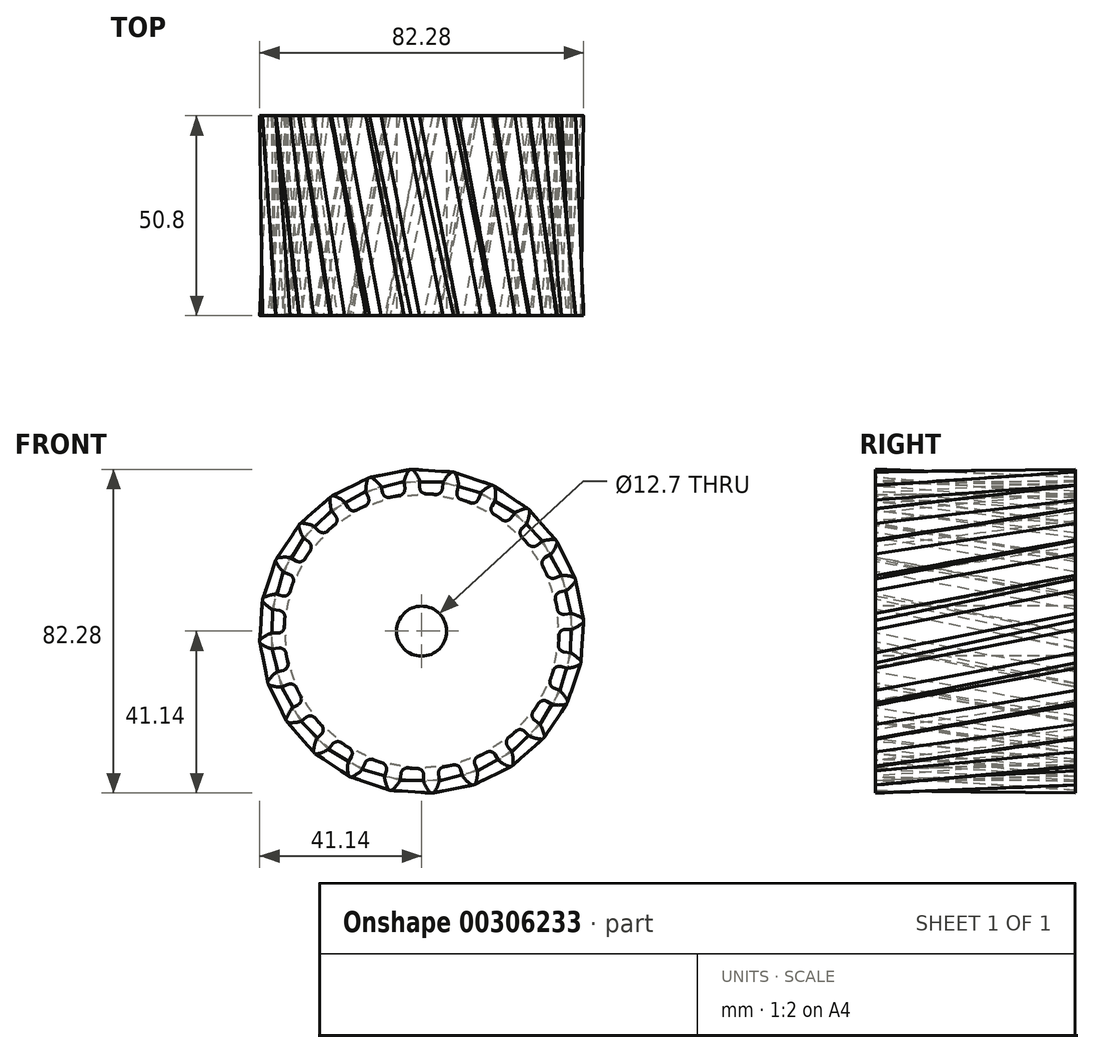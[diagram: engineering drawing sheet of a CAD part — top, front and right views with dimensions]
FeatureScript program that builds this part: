
annotation { "Feature Type Name" : "Feature", "Feature Type Description" : "" }
export const myFeature = defineFeature(function(context is Context, id is Id, definition is map)
    precondition{}
    {
        {
            var Q0;
            Q0=qCreatedBy(makeId("Front.planeOp"),FACE);
            var sketch = newSketch(context, id + "F0", { "sketchPlane" : qUnion([Q0])});
            skArc(sketch, "E0", {"start": v(-5.62, 34.47) * mm, "mid": v(-6.82, 34.25) * mm, "end": v(-8, 34) * mm});
            skLineSegment(sketch, "E1", {"start": v(0, 0) * mm, "end": v(-3.65, 55.58) * mm, "construction": true});
            skLineSegment(sketch, "E2", {"start": v(-2.53, 41.14) * mm, "end": v(-2.7, 41.14) * mm});
            skLineSegment(sketch, "E3", {"start": v(-0.5, 38.26) * mm, "end": v(-0.49, 36.5) * mm});
            skArc(sketch, "E4.trimOffspring", {"start": v(-0.5, 38.26) * mm, "mid": v(-1.2, 39.69) * mm, "end": v(-2.14, 40.97) * mm});
            skLineSegment(sketch, "E5.MirrorCS", {"start": v(-2.87, 41.12) * mm, "end": v(-2.7, 41.14) * mm});
            skArc(sketch, "E6.MirrorCS", {"start": v(-4.5, 38) * mm, "mid": v(-4, 39.5) * mm, "end": v(-3.23, 40.9) * mm});
            skLineSegment(sketch, "E7.MirrorCS", {"start": v(-4.5, 38) * mm, "end": v(-4.29, 36.25) * mm});
            skPoint(sketch, "E8.orphan", {"position": v(-3.92, 33.37) * mm});
            skPoint(sketch, "E9.orphan", {"position": v(-0.48, 33.6) * mm});
            skPoint(sketch, "E10.visualSharp", {"position": v(-4.08, 34.69) * mm});
            skArc(sketch, "E10.filletArc", {"start": v(-5.62, 34.47) * mm, "mid": v(-4.59, 35.1) * mm, "end": v(-4.29, 36.25) * mm});
            skPoint(sketch, "E11.visualSharp", {"position": v(-0.48, 34.92) * mm});
            skArc(sketch, "E11.filletArc", {"start": v(-0.49, 36.5) * mm, "mid": v(-0.03, 35.4) * mm, "end": v(1.06, 34.9) * mm});
            skPoint(sketch, "E12.visualSharp", {"position": v(-2.3, 41.14) * mm});
            skArc(sketch, "E12.filletArc", {"start": v(-2.14, 40.97) * mm, "mid": v(-2.32, 41.1) * mm, "end": v(-2.53, 41.14) * mm});
            skPoint(sketch, "E13.visualSharp", {"position": v(-3.1, 41.1) * mm});
            skArc(sketch, "E13.filletArc", {"start": v(-2.87, 41.12) * mm, "mid": v(-3.07, 41.05) * mm, "end": v(-3.23, 40.9) * mm});
            skLineSegment(sketch, "E14.1.0", {"start": v(-13.42, 38.98) * mm, "end": v(-13.26, 39.04) * mm});
            skArc(sketch, "E14.1.1", {"start": v(-14.19, 35.54) * mm, "mid": v(-14.08, 37.12) * mm, "end": v(-13.7, 38.67) * mm});
            skLineSegment(sketch, "E14.1.2", {"start": v(-13.09, 39.09) * mm, "end": v(-13.26, 39.04) * mm});
            skArc(sketch, "E14.1.3", {"start": v(-14.35, 31.84) * mm, "mid": v(-13.52, 32.7) * mm, "end": v(-13.52, 33.9) * mm});
            skLineSegment(sketch, "E14.1.4", {"start": v(-14.19, 35.54) * mm, "end": v(-13.52, 33.9) * mm});
            skArc(sketch, "E14.1.5", {"start": v(-10.38, 36.83) * mm, "mid": v(-11.43, 38.02) * mm, "end": v(-12.67, 39.02) * mm});
            skLineSegment(sketch, "E14.1.6", {"start": v(-10.38, 36.83) * mm, "end": v(-9.92, 35.13) * mm});
            skArc(sketch, "E14.1.7", {"start": v(-9.92, 35.13) * mm, "mid": v(-9.2, 34.18) * mm, "end": v(-8, 34) * mm});
            skArc(sketch, "E14.1.8", {"start": v(-12.67, 39.02) * mm, "mid": v(-12.87, 39.1) * mm, "end": v(-13.09, 39.09) * mm});
            skArc(sketch, "E14.1.9", {"start": v(-13.42, 38.98) * mm, "mid": v(-13.6, 38.85) * mm, "end": v(-13.7, 38.67) * mm});
            skLineSegment(sketch, "E14.2.0", {"start": v(-23.05, 34.18) * mm, "end": v(-22.9, 34.28) * mm});
            skArc(sketch, "E14.2.1", {"start": v(-22.9, 30.65) * mm, "mid": v(-23.2, 32.21) * mm, "end": v(-23.24, 33.8) * mm});
            skLineSegment(sketch, "E14.2.2", {"start": v(-22.76, 34.37) * mm, "end": v(-22.9, 34.28) * mm});
            skArc(sketch, "E14.2.3", {"start": v(-22.1, 27.04) * mm, "mid": v(-21.52, 28.1) * mm, "end": v(-21.84, 29.25) * mm});
            skLineSegment(sketch, "E14.2.4", {"start": v(-22.9, 30.65) * mm, "end": v(-21.84, 29.25) * mm});
            skArc(sketch, "E14.2.5", {"start": v(-19.56, 32.89) * mm, "mid": v(-20.88, 33.77) * mm, "end": v(-22.34, 34.4) * mm});
            skLineSegment(sketch, "E14.2.6", {"start": v(-19.56, 32.89) * mm, "end": v(-18.67, 31.37) * mm});
            skArc(sketch, "E14.2.7", {"start": v(-18.67, 31.37) * mm, "mid": v(-17.73, 30.63) * mm, "end": v(-16.53, 30.76) * mm});
            skArc(sketch, "E14.2.8", {"start": v(-22.34, 34.4) * mm, "mid": v(-22.55, 34.43) * mm, "end": v(-22.76, 34.37) * mm});
            skArc(sketch, "E14.2.9", {"start": v(-23.05, 34.18) * mm, "mid": v(-23.19, 34.01) * mm, "end": v(-23.24, 33.8) * mm});
            skLineSegment(sketch, "E14.3.0", {"start": v(-31.1, 27.05) * mm, "end": v(-31, 27.18) * mm});
            skArc(sketch, "E14.3.1", {"start": v(-30.06, 23.68) * mm, "mid": v(-30.75, 25.1) * mm, "end": v(-31.2, 26.64) * mm});
            skLineSegment(sketch, "E14.3.2", {"start": v(-30.88, 27.3) * mm, "end": v(-31, 27.18) * mm});
            skArc(sketch, "E14.3.3", {"start": v(-28.34, 20.4) * mm, "mid": v(-28.06, 21.57) * mm, "end": v(-28.66, 22.6) * mm});
            skLineSegment(sketch, "E14.3.4", {"start": v(-30.06, 23.68) * mm, "end": v(-28.66, 22.6) * mm});
            skArc(sketch, "E14.3.5", {"start": v(-27.4, 26.7) * mm, "mid": v(-28.91, 27.21) * mm, "end": v(-30.48, 27.45) * mm});
            skLineSegment(sketch, "E14.3.6", {"start": v(-27.4, 26.7) * mm, "end": v(-26.16, 25.47) * mm});
            skArc(sketch, "E14.3.7", {"start": v(-26.16, 25.47) * mm, "mid": v(-25.05, 25) * mm, "end": v(-23.93, 25.44) * mm});
            skArc(sketch, "E14.3.8", {"start": v(-30.48, 27.45) * mm, "mid": v(-30.7, 27.42) * mm, "end": v(-30.88, 27.3) * mm});
            skArc(sketch, "E14.3.9", {"start": v(-31.1, 27.05) * mm, "mid": v(-31.2, 26.85) * mm, "end": v(-31.2, 26.64) * mm});
            skLineSegment(sketch, "E14.4.0", {"start": v(-37.05, 18.07) * mm, "end": v(-36.98, 18.23) * mm});
            skArc(sketch, "E14.4.1", {"start": v(-35.16, 15.1) * mm, "mid": v(-36.2, 16.3) * mm, "end": v(-37.03, 17.65) * mm});
            skLineSegment(sketch, "E14.4.2", {"start": v(-36.9, 18.38) * mm, "end": v(-36.98, 18.23) * mm});
            skArc(sketch, "E14.4.3", {"start": v(-32.66, 12.37) * mm, "mid": v(-32.69, 13.57) * mm, "end": v(-33.54, 14.42) * mm});
            skLineSegment(sketch, "E14.4.4", {"start": v(-35.16, 15.1) * mm, "end": v(-33.54, 14.42) * mm});
            skArc(sketch, "E14.4.5", {"start": v(-33.38, 18.7) * mm, "mid": v(-34.97, 18.8) * mm, "end": v(-36.55, 18.63) * mm});
            skLineSegment(sketch, "E14.4.6", {"start": v(-33.38, 18.7) * mm, "end": v(-31.86, 17.83) * mm});
            skArc(sketch, "E14.4.7", {"start": v(-31.86, 17.83) * mm, "mid": v(-30.67, 17.67) * mm, "end": v(-29.7, 18.38) * mm});
            skArc(sketch, "E14.4.8", {"start": v(-36.55, 18.63) * mm, "mid": v(-36.75, 18.54) * mm, "end": v(-36.9, 18.38) * mm});
            skArc(sketch, "E14.4.9", {"start": v(-37.05, 18.07) * mm, "mid": v(-37.08, 17.86) * mm, "end": v(-37.03, 17.65) * mm});
            skLineSegment(sketch, "E14.5.0", {"start": v(-40.46, 7.87) * mm, "end": v(-40.44, 8.04) * mm});
            skArc(sketch, "E14.5.1", {"start": v(-37.87, 5.48) * mm, "mid": v(-39.19, 6.37) * mm, "end": v(-40.34, 7.47) * mm});
            skLineSegment(sketch, "E14.5.2", {"start": v(-40.4, 8.2) * mm, "end": v(-40.44, 8.04) * mm});
            skArc(sketch, "E14.5.3", {"start": v(-34.75, 3.5) * mm, "mid": v(-35.09, 4.65) * mm, "end": v(-36.13, 5.24) * mm});
            skLineSegment(sketch, "E14.5.4", {"start": v(-37.87, 5.48) * mm, "end": v(-36.13, 5.24) * mm});
            skArc(sketch, "E14.5.5", {"start": v(-37.09, 9.43) * mm, "mid": v(-38.64, 9.1) * mm, "end": v(-40.13, 8.53) * mm});
            skLineSegment(sketch, "E14.5.6", {"start": v(-37.09, 9.43) * mm, "end": v(-35.38, 8.98) * mm});
            skArc(sketch, "E14.5.7", {"start": v(-35.38, 8.98) * mm, "mid": v(-34.2, 9.13) * mm, "end": v(-33.44, 10.06) * mm});
            skArc(sketch, "E14.5.8", {"start": v(-40.13, 8.53) * mm, "mid": v(-40.3, 8.4) * mm, "end": v(-40.4, 8.2) * mm});
            skArc(sketch, "E14.5.9", {"start": v(-40.46, 7.87) * mm, "mid": v(-40.44, 7.66) * mm, "end": v(-40.34, 7.47) * mm});
            skLineSegment(sketch, "E14.6.0", {"start": v(-41.12, -2.87) * mm, "end": v(-41.14, -2.7) * mm});
            skArc(sketch, "E14.6.1", {"start": v(-38, -4.5) * mm, "mid": v(-39.5, -4) * mm, "end": v(-40.9, -3.23) * mm});
            skLineSegment(sketch, "E14.6.2", {"start": v(-41.14, -2.53) * mm, "end": v(-41.14, -2.7) * mm});
            skArc(sketch, "E14.6.3", {"start": v(-34.47, -5.62) * mm, "mid": v(-35.1, -4.59) * mm, "end": v(-36.25, -4.29) * mm});
            skLineSegment(sketch, "E14.6.4", {"start": v(-38, -4.5) * mm, "end": v(-36.25, -4.29) * mm});
            skArc(sketch, "E14.6.5", {"start": v(-38.26, -0.5) * mm, "mid": v(-39.69, -1.2) * mm, "end": v(-40.97, -2.14) * mm});
            skLineSegment(sketch, "E14.6.6", {"start": v(-38.26, -0.5) * mm, "end": v(-36.5, -0.49) * mm});
            skArc(sketch, "E14.6.7", {"start": v(-36.5, -0.49) * mm, "mid": v(-35.4, -0.03) * mm, "end": v(-34.9, 1.06) * mm});
            skArc(sketch, "E14.6.8", {"start": v(-40.97, -2.14) * mm, "mid": v(-41.1, -2.32) * mm, "end": v(-41.14, -2.53) * mm});
            skArc(sketch, "E14.6.9", {"start": v(-41.12, -2.87) * mm, "mid": v(-41.05, -3.07) * mm, "end": v(-40.9, -3.23) * mm});
            skLineSegment(sketch, "E14.7.0", {"start": v(-38.98, -13.42) * mm, "end": v(-39.04, -13.26) * mm});
            skArc(sketch, "E14.7.1", {"start": v(-35.54, -14.19) * mm, "mid": v(-37.12, -14.08) * mm, "end": v(-38.67, -13.7) * mm});
            skLineSegment(sketch, "E14.7.2", {"start": v(-39.09, -13.09) * mm, "end": v(-39.04, -13.26) * mm});
            skArc(sketch, "E14.7.3", {"start": v(-31.84, -14.35) * mm, "mid": v(-32.7, -13.52) * mm, "end": v(-33.9, -13.52) * mm});
            skLineSegment(sketch, "E14.7.4", {"start": v(-35.54, -14.19) * mm, "end": v(-33.9, -13.52) * mm});
            skArc(sketch, "E14.7.5", {"start": v(-36.83, -10.38) * mm, "mid": v(-38.02, -11.43) * mm, "end": v(-39.02, -12.67) * mm});
            skLineSegment(sketch, "E14.7.6", {"start": v(-36.83, -10.38) * mm, "end": v(-35.13, -9.92) * mm});
            skArc(sketch, "E14.7.7", {"start": v(-35.13, -9.92) * mm, "mid": v(-34.18, -9.2) * mm, "end": v(-34, -8) * mm});
            skArc(sketch, "E14.7.8", {"start": v(-39.02, -12.67) * mm, "mid": v(-39.1, -12.87) * mm, "end": v(-39.09, -13.09) * mm});
            skArc(sketch, "E14.7.9", {"start": v(-38.98, -13.42) * mm, "mid": v(-38.85, -13.6) * mm, "end": v(-38.67, -13.7) * mm});
            skLineSegment(sketch, "E14.8.0", {"start": v(-34.18, -23.05) * mm, "end": v(-34.28, -22.9) * mm});
            skArc(sketch, "E14.8.1", {"start": v(-30.65, -22.9) * mm, "mid": v(-32.21, -23.2) * mm, "end": v(-33.8, -23.24) * mm});
            skLineSegment(sketch, "E14.8.2", {"start": v(-34.37, -22.76) * mm, "end": v(-34.28, -22.9) * mm});
            skArc(sketch, "E14.8.3", {"start": v(-27.04, -22.1) * mm, "mid": v(-28.1, -21.52) * mm, "end": v(-29.25, -21.84) * mm});
            skLineSegment(sketch, "E14.8.4", {"start": v(-30.65, -22.9) * mm, "end": v(-29.25, -21.84) * mm});
            skArc(sketch, "E14.8.5", {"start": v(-32.89, -19.56) * mm, "mid": v(-33.77, -20.88) * mm, "end": v(-34.4, -22.34) * mm});
            skLineSegment(sketch, "E14.8.6", {"start": v(-32.89, -19.56) * mm, "end": v(-31.37, -18.67) * mm});
            skArc(sketch, "E14.8.7", {"start": v(-31.37, -18.67) * mm, "mid": v(-30.63, -17.73) * mm, "end": v(-30.76, -16.53) * mm});
            skArc(sketch, "E14.8.8", {"start": v(-34.4, -22.34) * mm, "mid": v(-34.43, -22.55) * mm, "end": v(-34.37, -22.76) * mm});
            skArc(sketch, "E14.8.9", {"start": v(-34.18, -23.05) * mm, "mid": v(-34.01, -23.19) * mm, "end": v(-33.8, -23.24) * mm});
            skLineSegment(sketch, "E14.9.0", {"start": v(-27.05, -31.1) * mm, "end": v(-27.18, -31) * mm});
            skArc(sketch, "E14.9.1", {"start": v(-23.68, -30.06) * mm, "mid": v(-25.1, -30.75) * mm, "end": v(-26.64, -31.2) * mm});
            skLineSegment(sketch, "E14.9.2", {"start": v(-27.3, -30.88) * mm, "end": v(-27.18, -31) * mm});
            skArc(sketch, "E14.9.3", {"start": v(-20.4, -28.34) * mm, "mid": v(-21.57, -28.06) * mm, "end": v(-22.6, -28.66) * mm});
            skLineSegment(sketch, "E14.9.4", {"start": v(-23.68, -30.06) * mm, "end": v(-22.6, -28.66) * mm});
            skArc(sketch, "E14.9.5", {"start": v(-26.7, -27.4) * mm, "mid": v(-27.21, -28.91) * mm, "end": v(-27.45, -30.48) * mm});
            skLineSegment(sketch, "E14.9.6", {"start": v(-26.7, -27.4) * mm, "end": v(-25.47, -26.16) * mm});
            skArc(sketch, "E14.9.7", {"start": v(-25.47, -26.16) * mm, "mid": v(-25, -25.05) * mm, "end": v(-25.44, -23.93) * mm});
            skArc(sketch, "E14.9.8", {"start": v(-27.45, -30.48) * mm, "mid": v(-27.42, -30.7) * mm, "end": v(-27.3, -30.88) * mm});
            skArc(sketch, "E14.9.9", {"start": v(-27.05, -31.1) * mm, "mid": v(-26.85, -31.2) * mm, "end": v(-26.64, -31.2) * mm});
            skLineSegment(sketch, "E14.10.0", {"start": v(-18.07, -37.05) * mm, "end": v(-18.23, -36.98) * mm});
            skArc(sketch, "E14.10.1", {"start": v(-15.1, -35.16) * mm, "mid": v(-16.3, -36.2) * mm, "end": v(-17.65, -37.03) * mm});
            skLineSegment(sketch, "E14.10.2", {"start": v(-18.38, -36.9) * mm, "end": v(-18.23, -36.98) * mm});
            skArc(sketch, "E14.10.3", {"start": v(-12.37, -32.66) * mm, "mid": v(-13.57, -32.69) * mm, "end": v(-14.42, -33.54) * mm});
            skLineSegment(sketch, "E14.10.4", {"start": v(-15.1, -35.16) * mm, "end": v(-14.42, -33.54) * mm});
            skArc(sketch, "E14.10.5", {"start": v(-18.7, -33.38) * mm, "mid": v(-18.8, -34.97) * mm, "end": v(-18.63, -36.55) * mm});
            skLineSegment(sketch, "E14.10.6", {"start": v(-18.7, -33.38) * mm, "end": v(-17.83, -31.86) * mm});
            skArc(sketch, "E14.10.7", {"start": v(-17.83, -31.86) * mm, "mid": v(-17.67, -30.67) * mm, "end": v(-18.38, -29.7) * mm});
            skArc(sketch, "E14.10.8", {"start": v(-18.63, -36.55) * mm, "mid": v(-18.54, -36.75) * mm, "end": v(-18.38, -36.9) * mm});
            skArc(sketch, "E14.10.9", {"start": v(-18.07, -37.05) * mm, "mid": v(-17.86, -37.08) * mm, "end": v(-17.65, -37.03) * mm});
            skLineSegment(sketch, "E14.11.0", {"start": v(-7.87, -40.46) * mm, "end": v(-8.04, -40.44) * mm});
            skArc(sketch, "E14.11.1", {"start": v(-5.48, -37.87) * mm, "mid": v(-6.37, -39.19) * mm, "end": v(-7.47, -40.34) * mm});
            skLineSegment(sketch, "E14.11.2", {"start": v(-8.2, -40.4) * mm, "end": v(-8.04, -40.44) * mm});
            skArc(sketch, "E14.11.3", {"start": v(-3.5, -34.75) * mm, "mid": v(-4.65, -35.09) * mm, "end": v(-5.24, -36.13) * mm});
            skLineSegment(sketch, "E14.11.4", {"start": v(-5.48, -37.87) * mm, "end": v(-5.24, -36.13) * mm});
            skArc(sketch, "E14.11.5", {"start": v(-9.43, -37.09) * mm, "mid": v(-9.1, -38.64) * mm, "end": v(-8.53, -40.13) * mm});
            skLineSegment(sketch, "E14.11.6", {"start": v(-9.43, -37.09) * mm, "end": v(-8.98, -35.38) * mm});
            skArc(sketch, "E14.11.7", {"start": v(-8.98, -35.38) * mm, "mid": v(-9.13, -34.2) * mm, "end": v(-10.06, -33.44) * mm});
            skArc(sketch, "E14.11.8", {"start": v(-8.53, -40.13) * mm, "mid": v(-8.4, -40.3) * mm, "end": v(-8.2, -40.4) * mm});
            skArc(sketch, "E14.11.9", {"start": v(-7.87, -40.46) * mm, "mid": v(-7.66, -40.44) * mm, "end": v(-7.47, -40.34) * mm});
            skLineSegment(sketch, "E14.12.0", {"start": v(2.87, -41.12) * mm, "end": v(2.7, -41.14) * mm});
            skArc(sketch, "E14.12.1", {"start": v(4.5, -38) * mm, "mid": v(4, -39.5) * mm, "end": v(3.23, -40.9) * mm});
            skLineSegment(sketch, "E14.12.2", {"start": v(2.53, -41.14) * mm, "end": v(2.7, -41.14) * mm});
            skArc(sketch, "E14.12.3", {"start": v(5.62, -34.47) * mm, "mid": v(4.59, -35.1) * mm, "end": v(4.29, -36.25) * mm});
            skLineSegment(sketch, "E14.12.4", {"start": v(4.5, -38) * mm, "end": v(4.29, -36.25) * mm});
            skArc(sketch, "E14.12.5", {"start": v(0.5, -38.26) * mm, "mid": v(1.2, -39.69) * mm, "end": v(2.14, -40.97) * mm});
            skLineSegment(sketch, "E14.12.6", {"start": v(0.5, -38.26) * mm, "end": v(0.49, -36.5) * mm});
            skArc(sketch, "E14.12.7", {"start": v(0.49, -36.5) * mm, "mid": v(0.03, -35.4) * mm, "end": v(-1.06, -34.9) * mm});
            skArc(sketch, "E14.12.8", {"start": v(2.14, -40.97) * mm, "mid": v(2.32, -41.1) * mm, "end": v(2.53, -41.14) * mm});
            skArc(sketch, "E14.12.9", {"start": v(2.87, -41.12) * mm, "mid": v(3.07, -41.05) * mm, "end": v(3.23, -40.9) * mm});
            skLineSegment(sketch, "E14.13.0", {"start": v(13.42, -38.98) * mm, "end": v(13.26, -39.04) * mm});
            skArc(sketch, "E14.13.1", {"start": v(14.19, -35.54) * mm, "mid": v(14.08, -37.12) * mm, "end": v(13.7, -38.67) * mm});
            skLineSegment(sketch, "E14.13.2", {"start": v(13.09, -39.09) * mm, "end": v(13.26, -39.04) * mm});
            skArc(sketch, "E14.13.3", {"start": v(14.35, -31.84) * mm, "mid": v(13.52, -32.7) * mm, "end": v(13.52, -33.9) * mm});
            skLineSegment(sketch, "E14.13.4", {"start": v(14.19, -35.54) * mm, "end": v(13.52, -33.9) * mm});
            skArc(sketch, "E14.13.5", {"start": v(10.38, -36.83) * mm, "mid": v(11.43, -38.02) * mm, "end": v(12.67, -39.02) * mm});
            skLineSegment(sketch, "E14.13.6", {"start": v(10.38, -36.83) * mm, "end": v(9.92, -35.13) * mm});
            skArc(sketch, "E14.13.7", {"start": v(9.92, -35.13) * mm, "mid": v(9.2, -34.18) * mm, "end": v(8, -34) * mm});
            skArc(sketch, "E14.13.8", {"start": v(12.67, -39.02) * mm, "mid": v(12.87, -39.1) * mm, "end": v(13.09, -39.09) * mm});
            skArc(sketch, "E14.13.9", {"start": v(13.42, -38.98) * mm, "mid": v(13.6, -38.85) * mm, "end": v(13.7, -38.67) * mm});
            skLineSegment(sketch, "E14.14.0", {"start": v(23.05, -34.18) * mm, "end": v(22.9, -34.28) * mm});
            skArc(sketch, "E14.14.1", {"start": v(22.9, -30.65) * mm, "mid": v(23.2, -32.21) * mm, "end": v(23.24, -33.8) * mm});
            skLineSegment(sketch, "E14.14.2", {"start": v(22.76, -34.37) * mm, "end": v(22.9, -34.28) * mm});
            skArc(sketch, "E14.14.3", {"start": v(22.1, -27.04) * mm, "mid": v(21.52, -28.1) * mm, "end": v(21.84, -29.25) * mm});
            skLineSegment(sketch, "E14.14.4", {"start": v(22.9, -30.65) * mm, "end": v(21.84, -29.25) * mm});
            skArc(sketch, "E14.14.5", {"start": v(19.56, -32.89) * mm, "mid": v(20.88, -33.77) * mm, "end": v(22.34, -34.4) * mm});
            skLineSegment(sketch, "E14.14.6", {"start": v(19.56, -32.89) * mm, "end": v(18.67, -31.37) * mm});
            skArc(sketch, "E14.14.7", {"start": v(18.67, -31.37) * mm, "mid": v(17.73, -30.63) * mm, "end": v(16.53, -30.76) * mm});
            skArc(sketch, "E14.14.8", {"start": v(22.34, -34.4) * mm, "mid": v(22.55, -34.43) * mm, "end": v(22.76, -34.37) * mm});
            skArc(sketch, "E14.14.9", {"start": v(23.05, -34.18) * mm, "mid": v(23.19, -34.01) * mm, "end": v(23.24, -33.8) * mm});
            skLineSegment(sketch, "E14.15.0", {"start": v(31.1, -27.05) * mm, "end": v(31, -27.18) * mm});
            skArc(sketch, "E14.15.1", {"start": v(30.06, -23.68) * mm, "mid": v(30.75, -25.1) * mm, "end": v(31.2, -26.64) * mm});
            skLineSegment(sketch, "E14.15.2", {"start": v(30.88, -27.3) * mm, "end": v(31, -27.18) * mm});
            skArc(sketch, "E14.15.3", {"start": v(28.34, -20.4) * mm, "mid": v(28.06, -21.57) * mm, "end": v(28.66, -22.6) * mm});
            skLineSegment(sketch, "E14.15.4", {"start": v(30.06, -23.68) * mm, "end": v(28.66, -22.6) * mm});
            skArc(sketch, "E14.15.5", {"start": v(27.4, -26.7) * mm, "mid": v(28.91, -27.21) * mm, "end": v(30.48, -27.45) * mm});
            skLineSegment(sketch, "E14.15.6", {"start": v(27.4, -26.7) * mm, "end": v(26.16, -25.47) * mm});
            skArc(sketch, "E14.15.7", {"start": v(26.16, -25.47) * mm, "mid": v(25.05, -25) * mm, "end": v(23.93, -25.44) * mm});
            skArc(sketch, "E14.15.8", {"start": v(30.48, -27.45) * mm, "mid": v(30.7, -27.42) * mm, "end": v(30.88, -27.3) * mm});
            skArc(sketch, "E14.15.9", {"start": v(31.1, -27.05) * mm, "mid": v(31.2, -26.85) * mm, "end": v(31.2, -26.64) * mm});
            skLineSegment(sketch, "E14.16.0", {"start": v(37.05, -18.07) * mm, "end": v(36.98, -18.23) * mm});
            skArc(sketch, "E14.16.1", {"start": v(35.16, -15.1) * mm, "mid": v(36.2, -16.3) * mm, "end": v(37.03, -17.65) * mm});
            skLineSegment(sketch, "E14.16.2", {"start": v(36.9, -18.38) * mm, "end": v(36.98, -18.23) * mm});
            skArc(sketch, "E14.16.3", {"start": v(32.66, -12.37) * mm, "mid": v(32.69, -13.57) * mm, "end": v(33.54, -14.42) * mm});
            skLineSegment(sketch, "E14.16.4", {"start": v(35.16, -15.1) * mm, "end": v(33.54, -14.42) * mm});
            skArc(sketch, "E14.16.5", {"start": v(33.38, -18.7) * mm, "mid": v(34.97, -18.8) * mm, "end": v(36.55, -18.63) * mm});
            skLineSegment(sketch, "E14.16.6", {"start": v(33.38, -18.7) * mm, "end": v(31.86, -17.83) * mm});
            skArc(sketch, "E14.16.7", {"start": v(31.86, -17.83) * mm, "mid": v(30.67, -17.67) * mm, "end": v(29.7, -18.38) * mm});
            skArc(sketch, "E14.16.8", {"start": v(36.55, -18.63) * mm, "mid": v(36.75, -18.54) * mm, "end": v(36.9, -18.38) * mm});
            skArc(sketch, "E14.16.9", {"start": v(37.05, -18.07) * mm, "mid": v(37.08, -17.86) * mm, "end": v(37.03, -17.65) * mm});
            skLineSegment(sketch, "E14.17.0", {"start": v(40.46, -7.87) * mm, "end": v(40.44, -8.04) * mm});
            skArc(sketch, "E14.17.1", {"start": v(37.87, -5.48) * mm, "mid": v(39.19, -6.37) * mm, "end": v(40.34, -7.47) * mm});
            skLineSegment(sketch, "E14.17.2", {"start": v(40.4, -8.2) * mm, "end": v(40.44, -8.04) * mm});
            skArc(sketch, "E14.17.3", {"start": v(34.75, -3.5) * mm, "mid": v(35.09, -4.65) * mm, "end": v(36.13, -5.24) * mm});
            skLineSegment(sketch, "E14.17.4", {"start": v(37.87, -5.48) * mm, "end": v(36.13, -5.24) * mm});
            skArc(sketch, "E14.17.5", {"start": v(37.09, -9.43) * mm, "mid": v(38.64, -9.1) * mm, "end": v(40.13, -8.53) * mm});
            skLineSegment(sketch, "E14.17.6", {"start": v(37.09, -9.43) * mm, "end": v(35.38, -8.98) * mm});
            skArc(sketch, "E14.17.7", {"start": v(35.38, -8.98) * mm, "mid": v(34.2, -9.13) * mm, "end": v(33.44, -10.06) * mm});
            skArc(sketch, "E14.17.8", {"start": v(40.13, -8.53) * mm, "mid": v(40.3, -8.4) * mm, "end": v(40.4, -8.2) * mm});
            skArc(sketch, "E14.17.9", {"start": v(40.46, -7.87) * mm, "mid": v(40.44, -7.66) * mm, "end": v(40.34, -7.47) * mm});
            skLineSegment(sketch, "E14.18.0", {"start": v(41.12, 2.87) * mm, "end": v(41.14, 2.7) * mm});
            skArc(sketch, "E14.18.1", {"start": v(38, 4.5) * mm, "mid": v(39.5, 4) * mm, "end": v(40.9, 3.23) * mm});
            skLineSegment(sketch, "E14.18.2", {"start": v(41.14, 2.53) * mm, "end": v(41.14, 2.7) * mm});
            skArc(sketch, "E14.18.3", {"start": v(34.47, 5.62) * mm, "mid": v(35.1, 4.59) * mm, "end": v(36.25, 4.29) * mm});
            skLineSegment(sketch, "E14.18.4", {"start": v(38, 4.5) * mm, "end": v(36.25, 4.29) * mm});
            skArc(sketch, "E14.18.5", {"start": v(38.26, 0.5) * mm, "mid": v(39.69, 1.2) * mm, "end": v(40.97, 2.14) * mm});
            skLineSegment(sketch, "E14.18.6", {"start": v(38.26, 0.5) * mm, "end": v(36.5, 0.49) * mm});
            skArc(sketch, "E14.18.7", {"start": v(36.5, 0.49) * mm, "mid": v(35.4, 0.03) * mm, "end": v(34.9, -1.06) * mm});
            skArc(sketch, "E14.18.8", {"start": v(40.97, 2.14) * mm, "mid": v(41.1, 2.32) * mm, "end": v(41.14, 2.53) * mm});
            skArc(sketch, "E14.18.9", {"start": v(41.12, 2.87) * mm, "mid": v(41.05, 3.07) * mm, "end": v(40.9, 3.23) * mm});
            skLineSegment(sketch, "E14.19.0", {"start": v(38.98, 13.42) * mm, "end": v(39.04, 13.26) * mm});
            skArc(sketch, "E14.19.1", {"start": v(35.54, 14.19) * mm, "mid": v(37.12, 14.08) * mm, "end": v(38.67, 13.7) * mm});
            skLineSegment(sketch, "E14.19.2", {"start": v(39.09, 13.09) * mm, "end": v(39.04, 13.26) * mm});
            skArc(sketch, "E14.19.3", {"start": v(31.84, 14.35) * mm, "mid": v(32.7, 13.52) * mm, "end": v(33.9, 13.52) * mm});
            skLineSegment(sketch, "E14.19.4", {"start": v(35.54, 14.19) * mm, "end": v(33.9, 13.52) * mm});
            skArc(sketch, "E14.19.5", {"start": v(36.83, 10.38) * mm, "mid": v(38.02, 11.43) * mm, "end": v(39.02, 12.67) * mm});
            skLineSegment(sketch, "E14.19.6", {"start": v(36.83, 10.38) * mm, "end": v(35.13, 9.92) * mm});
            skArc(sketch, "E14.19.7", {"start": v(35.13, 9.92) * mm, "mid": v(34.18, 9.2) * mm, "end": v(34, 8) * mm});
            skArc(sketch, "E14.19.8", {"start": v(39.02, 12.67) * mm, "mid": v(39.1, 12.87) * mm, "end": v(39.09, 13.09) * mm});
            skArc(sketch, "E14.19.9", {"start": v(38.98, 13.42) * mm, "mid": v(38.85, 13.6) * mm, "end": v(38.67, 13.7) * mm});
            skLineSegment(sketch, "E14.20.0", {"start": v(34.18, 23.05) * mm, "end": v(34.28, 22.9) * mm});
            skArc(sketch, "E14.20.1", {"start": v(30.65, 22.9) * mm, "mid": v(32.21, 23.2) * mm, "end": v(33.8, 23.24) * mm});
            skLineSegment(sketch, "E14.20.2", {"start": v(34.37, 22.76) * mm, "end": v(34.28, 22.9) * mm});
            skArc(sketch, "E14.20.3", {"start": v(27.04, 22.1) * mm, "mid": v(28.1, 21.52) * mm, "end": v(29.25, 21.84) * mm});
            skLineSegment(sketch, "E14.20.4", {"start": v(30.65, 22.9) * mm, "end": v(29.25, 21.84) * mm});
            skArc(sketch, "E14.20.5", {"start": v(32.89, 19.56) * mm, "mid": v(33.77, 20.88) * mm, "end": v(34.4, 22.34) * mm});
            skLineSegment(sketch, "E14.20.6", {"start": v(32.89, 19.56) * mm, "end": v(31.37, 18.67) * mm});
            skArc(sketch, "E14.20.7", {"start": v(31.37, 18.67) * mm, "mid": v(30.63, 17.73) * mm, "end": v(30.76, 16.53) * mm});
            skArc(sketch, "E14.20.8", {"start": v(34.4, 22.34) * mm, "mid": v(34.43, 22.55) * mm, "end": v(34.37, 22.76) * mm});
            skArc(sketch, "E14.20.9", {"start": v(34.18, 23.05) * mm, "mid": v(34.01, 23.19) * mm, "end": v(33.8, 23.24) * mm});
            skLineSegment(sketch, "E14.21.0", {"start": v(27.05, 31.1) * mm, "end": v(27.18, 31) * mm});
            skArc(sketch, "E14.21.1", {"start": v(23.68, 30.06) * mm, "mid": v(25.1, 30.75) * mm, "end": v(26.64, 31.2) * mm});
            skLineSegment(sketch, "E14.21.2", {"start": v(27.3, 30.88) * mm, "end": v(27.18, 31) * mm});
            skArc(sketch, "E14.21.3", {"start": v(20.4, 28.34) * mm, "mid": v(21.57, 28.06) * mm, "end": v(22.6, 28.66) * mm});
            skLineSegment(sketch, "E14.21.4", {"start": v(23.68, 30.06) * mm, "end": v(22.6, 28.66) * mm});
            skArc(sketch, "E14.21.5", {"start": v(26.7, 27.4) * mm, "mid": v(27.21, 28.91) * mm, "end": v(27.45, 30.48) * mm});
            skLineSegment(sketch, "E14.21.6", {"start": v(26.7, 27.4) * mm, "end": v(25.47, 26.16) * mm});
            skArc(sketch, "E14.21.7", {"start": v(25.47, 26.16) * mm, "mid": v(25, 25.05) * mm, "end": v(25.44, 23.93) * mm});
            skArc(sketch, "E14.21.8", {"start": v(27.45, 30.48) * mm, "mid": v(27.42, 30.7) * mm, "end": v(27.3, 30.88) * mm});
            skArc(sketch, "E14.21.9", {"start": v(27.05, 31.1) * mm, "mid": v(26.85, 31.2) * mm, "end": v(26.64, 31.2) * mm});
            skLineSegment(sketch, "E14.22.0", {"start": v(18.07, 37.05) * mm, "end": v(18.23, 36.98) * mm});
            skArc(sketch, "E14.22.1", {"start": v(15.1, 35.16) * mm, "mid": v(16.3, 36.2) * mm, "end": v(17.65, 37.03) * mm});
            skLineSegment(sketch, "E14.22.2", {"start": v(18.38, 36.9) * mm, "end": v(18.23, 36.98) * mm});
            skArc(sketch, "E14.22.3", {"start": v(12.37, 32.66) * mm, "mid": v(13.57, 32.69) * mm, "end": v(14.42, 33.54) * mm});
            skLineSegment(sketch, "E14.22.4", {"start": v(15.1, 35.16) * mm, "end": v(14.42, 33.54) * mm});
            skArc(sketch, "E14.22.5", {"start": v(18.7, 33.38) * mm, "mid": v(18.8, 34.97) * mm, "end": v(18.63, 36.55) * mm});
            skLineSegment(sketch, "E14.22.6", {"start": v(18.7, 33.38) * mm, "end": v(17.83, 31.86) * mm});
            skArc(sketch, "E14.22.7", {"start": v(17.83, 31.86) * mm, "mid": v(17.67, 30.67) * mm, "end": v(18.38, 29.7) * mm});
            skArc(sketch, "E14.22.8", {"start": v(18.63, 36.55) * mm, "mid": v(18.54, 36.75) * mm, "end": v(18.38, 36.9) * mm});
            skArc(sketch, "E14.22.9", {"start": v(18.07, 37.05) * mm, "mid": v(17.86, 37.08) * mm, "end": v(17.65, 37.03) * mm});
            skLineSegment(sketch, "E14.23.0", {"start": v(7.87, 40.46) * mm, "end": v(8.04, 40.44) * mm});
            skArc(sketch, "E14.23.1", {"start": v(5.48, 37.87) * mm, "mid": v(6.37, 39.19) * mm, "end": v(7.47, 40.34) * mm});
            skLineSegment(sketch, "E14.23.2", {"start": v(8.2, 40.4) * mm, "end": v(8.04, 40.44) * mm});
            skArc(sketch, "E14.23.3", {"start": v(3.5, 34.75) * mm, "mid": v(4.65, 35.09) * mm, "end": v(5.24, 36.13) * mm});
            skLineSegment(sketch, "E14.23.4", {"start": v(5.48, 37.87) * mm, "end": v(5.24, 36.13) * mm});
            skArc(sketch, "E14.23.5", {"start": v(9.43, 37.09) * mm, "mid": v(9.1, 38.64) * mm, "end": v(8.53, 40.13) * mm});
            skLineSegment(sketch, "E14.23.6", {"start": v(9.43, 37.09) * mm, "end": v(8.98, 35.38) * mm});
            skArc(sketch, "E14.23.7", {"start": v(8.98, 35.38) * mm, "mid": v(9.13, 34.2) * mm, "end": v(10.06, 33.44) * mm});
            skArc(sketch, "E14.23.8", {"start": v(8.53, 40.13) * mm, "mid": v(8.4, 40.3) * mm, "end": v(8.2, 40.4) * mm});
            skArc(sketch, "E14.23.9", {"start": v(7.87, 40.46) * mm, "mid": v(7.66, 40.44) * mm, "end": v(7.47, 40.34) * mm});
            skArc(sketch, "E15.trimOffspring", {"start": v(-14.35, 31.84) * mm, "mid": v(-15.45, 31.32) * mm, "end": v(-16.53, 30.76) * mm});
            skArc(sketch, "E16.trimOffspring", {"start": v(-22.1, 27.04) * mm, "mid": v(-23.03, 26.26) * mm, "end": v(-23.93, 25.44) * mm});
            skArc(sketch, "E17.trimOffspring", {"start": v(-28.34, 20.4) * mm, "mid": v(-29.04, 19.4) * mm, "end": v(-29.7, 18.38) * mm});
            skArc(sketch, "E18.trimOffspring", {"start": v(-32.66, 12.37) * mm, "mid": v(-33.07, 11.22) * mm, "end": v(-33.44, 10.06) * mm});
            skArc(sketch, "E19.trimOffspring", {"start": v(-34.75, 3.5) * mm, "mid": v(-34.85, 2.28) * mm, "end": v(-34.9, 1.06) * mm});
            skArc(sketch, "E20.trimOffspring", {"start": v(-34.47, -5.62) * mm, "mid": v(-34.25, -6.82) * mm, "end": v(-34, -8) * mm});
            skArc(sketch, "E21.trimOffspring", {"start": v(-31.84, -14.35) * mm, "mid": v(-31.32, -15.45) * mm, "end": v(-30.76, -16.53) * mm});
            skArc(sketch, "E22.trimOffspring", {"start": v(-27.04, -22.1) * mm, "mid": v(-26.26, -23.03) * mm, "end": v(-25.44, -23.93) * mm});
            skArc(sketch, "E23.trimOffspring", {"start": v(-20.4, -28.34) * mm, "mid": v(-19.4, -29.04) * mm, "end": v(-18.38, -29.7) * mm});
            skArc(sketch, "E24.trimOffspring", {"start": v(-12.37, -32.66) * mm, "mid": v(-11.22, -33.07) * mm, "end": v(-10.06, -33.44) * mm});
            skArc(sketch, "E25.trimOffspring", {"start": v(-3.5, -34.75) * mm, "mid": v(-2.28, -34.85) * mm, "end": v(-1.06, -34.9) * mm});
            skArc(sketch, "E26.trimOffspring", {"start": v(5.62, -34.47) * mm, "mid": v(6.82, -34.25) * mm, "end": v(8, -34) * mm});
            skArc(sketch, "E27.trimOffspring", {"start": v(14.35, -31.84) * mm, "mid": v(15.45, -31.32) * mm, "end": v(16.53, -30.76) * mm});
            skArc(sketch, "E28.trimOffspring", {"start": v(22.1, -27.04) * mm, "mid": v(23.03, -26.26) * mm, "end": v(23.93, -25.44) * mm});
            skArc(sketch, "E29.trimOffspring", {"start": v(3.5, 34.75) * mm, "mid": v(2.28, 34.85) * mm, "end": v(1.06, 34.9) * mm});
            skArc(sketch, "E30.trimOffspring", {"start": v(12.37, 32.66) * mm, "mid": v(11.22, 33.07) * mm, "end": v(10.06, 33.44) * mm});
            skArc(sketch, "E31.trimOffspring", {"start": v(20.4, 28.34) * mm, "mid": v(19.4, 29.04) * mm, "end": v(18.38, 29.7) * mm});
            skArc(sketch, "E32.trimOffspring", {"start": v(27.04, 22.1) * mm, "mid": v(26.26, 23.03) * mm, "end": v(25.44, 23.93) * mm});
            skArc(sketch, "E33.trimOffspring", {"start": v(31.84, 14.35) * mm, "mid": v(31.32, 15.45) * mm, "end": v(30.76, 16.53) * mm});
            skArc(sketch, "E34.trimOffspring", {"start": v(34.47, 5.62) * mm, "mid": v(34.25, 6.82) * mm, "end": v(34, 8) * mm});
            skArc(sketch, "E35.trimOffspring", {"start": v(34.75, -3.5) * mm, "mid": v(34.85, -2.28) * mm, "end": v(34.9, -1.06) * mm});
            skArc(sketch, "E36.trimOffspring", {"start": v(32.66, -12.37) * mm, "mid": v(33.07, -11.22) * mm, "end": v(33.44, -10.06) * mm});
            skArc(sketch, "E37.trimOffspring", {"start": v(28.34, -20.4) * mm, "mid": v(29.04, -19.4) * mm, "end": v(29.7, -18.38) * mm});
            skSolve(sketch);
        }
        {
            var Q0;
            Q0=makeQuery(id+"F0.imprint","IMPRINT",FACE,{"disambiguationData":[TD([[makeQuery(id+"F0.imprint","IMPRINT",EDGE,{"derivedFrom":sQuery(id+"F0.wireOp",EDGE,"E0")}),1.0]])]});
            cPlane(context, id + "F1", {"entities" : qUnion([Q0]), "cplaneType" : CPlaneType.OFFSET, "offset" : 50.8 * mm, "width" : 152.4 * mm, "height" : 152.4 * mm});
        }
        {
            var Q0;
            Q0=qCreatedBy(id+"F1.planeOp",FACE);
            var sketch = newSketch(context, id + "F2", { "sketchPlane" : qUnion([Q0])});
            skArc(sketch, "E38", {"start": v(-5.62, 34.47) * mm, "mid": v(-6.82, 34.25) * mm, "end": v(-8, 34) * mm});
            skLineSegment(sketch, "E39", {"start": v(0, 0) * mm, "end": v(-3.98, 60.7) * mm, "construction": true});
            skLineSegment(sketch, "E40", {"start": v(-2.53, 41.14) * mm, "end": v(-2.7, 41.14) * mm});
            skLineSegment(sketch, "E41", {"start": v(-0.5, 38.26) * mm, "end": v(-0.49, 36.5) * mm});
            skArc(sketch, "E42.trimOffspring", {"start": v(-0.5, 38.26) * mm, "mid": v(-1.2, 39.69) * mm, "end": v(-2.14, 40.97) * mm});
            skLineSegment(sketch, "E43.MirrorCS", {"start": v(-2.87, 41.12) * mm, "end": v(-2.7, 41.14) * mm});
            skArc(sketch, "E44.MirrorCS", {"start": v(-4.5, 38) * mm, "mid": v(-4, 39.5) * mm, "end": v(-3.23, 40.9) * mm});
            skLineSegment(sketch, "E45.MirrorCS", {"start": v(-4.5, 38) * mm, "end": v(-4.29, 36.25) * mm});
            skPoint(sketch, "E46.orphan", {"position": v(-3.91, 33.33) * mm});
            skPoint(sketch, "E47.orphan", {"position": v(-0.48, 33.56) * mm});
            skPoint(sketch, "E48.visualSharp", {"position": v(-3.1, 41.1) * mm});
            skArc(sketch, "E48.filletArc", {"start": v(-2.87, 41.12) * mm, "mid": v(-3.07, 41.05) * mm, "end": v(-3.23, 40.9) * mm});
            skPoint(sketch, "E49.visualSharp", {"position": v(-4.08, 34.69) * mm});
            skArc(sketch, "E49.filletArc", {"start": v(-5.62, 34.47) * mm, "mid": v(-4.59, 35.1) * mm, "end": v(-4.29, 36.25) * mm});
            skPoint(sketch, "E50.visualSharp", {"position": v(-2.3, 41.14) * mm});
            skArc(sketch, "E50.filletArc", {"start": v(-2.14, 40.97) * mm, "mid": v(-2.32, 41.1) * mm, "end": v(-2.53, 41.14) * mm});
            skPoint(sketch, "E51.visualSharp", {"position": v(-0.48, 34.92) * mm});
            skArc(sketch, "E51.filletArc", {"start": v(-0.49, 36.5) * mm, "mid": v(-0.03, 35.4) * mm, "end": v(1.06, 34.9) * mm});
            skArc(sketch, "E52.1.0", {"start": v(-14.35, 31.84) * mm, "mid": v(-13.52, 32.7) * mm, "end": v(-13.52, 33.9) * mm});
            skLineSegment(sketch, "E52.1.1", {"start": v(-14.19, 35.54) * mm, "end": v(-13.52, 33.9) * mm});
            skArc(sketch, "E52.1.2", {"start": v(-14.19, 35.54) * mm, "mid": v(-14.08, 37.12) * mm, "end": v(-13.7, 38.67) * mm});
            skLineSegment(sketch, "E52.1.3", {"start": v(-13.42, 38.98) * mm, "end": v(-13.26, 39.04) * mm});
            skArc(sketch, "E52.1.4", {"start": v(-13.42, 38.98) * mm, "mid": v(-13.6, 38.85) * mm, "end": v(-13.7, 38.67) * mm});
            skLineSegment(sketch, "E52.1.5", {"start": v(-13.09, 39.09) * mm, "end": v(-13.26, 39.04) * mm});
            skArc(sketch, "E52.1.6", {"start": v(-12.67, 39.02) * mm, "mid": v(-12.87, 39.1) * mm, "end": v(-13.09, 39.09) * mm});
            skArc(sketch, "E52.1.7", {"start": v(-10.38, 36.83) * mm, "mid": v(-11.43, 38.02) * mm, "end": v(-12.67, 39.02) * mm});
            skLineSegment(sketch, "E52.1.8", {"start": v(-10.38, 36.83) * mm, "end": v(-9.92, 35.13) * mm});
            skArc(sketch, "E52.1.9", {"start": v(-9.92, 35.13) * mm, "mid": v(-9.2, 34.18) * mm, "end": v(-8, 34) * mm});
            skArc(sketch, "E52.2.0", {"start": v(-22.1, 27.04) * mm, "mid": v(-21.52, 28.1) * mm, "end": v(-21.84, 29.25) * mm});
            skLineSegment(sketch, "E52.2.1", {"start": v(-22.9, 30.65) * mm, "end": v(-21.84, 29.25) * mm});
            skArc(sketch, "E52.2.2", {"start": v(-22.9, 30.65) * mm, "mid": v(-23.2, 32.21) * mm, "end": v(-23.24, 33.8) * mm});
            skLineSegment(sketch, "E52.2.3", {"start": v(-23.05, 34.18) * mm, "end": v(-22.9, 34.28) * mm});
            skArc(sketch, "E52.2.4", {"start": v(-23.05, 34.18) * mm, "mid": v(-23.19, 34.01) * mm, "end": v(-23.24, 33.8) * mm});
            skLineSegment(sketch, "E52.2.5", {"start": v(-22.76, 34.37) * mm, "end": v(-22.9, 34.28) * mm});
            skArc(sketch, "E52.2.6", {"start": v(-22.34, 34.4) * mm, "mid": v(-22.55, 34.43) * mm, "end": v(-22.76, 34.37) * mm});
            skArc(sketch, "E52.2.7", {"start": v(-19.56, 32.89) * mm, "mid": v(-20.88, 33.77) * mm, "end": v(-22.34, 34.4) * mm});
            skLineSegment(sketch, "E52.2.8", {"start": v(-19.56, 32.89) * mm, "end": v(-18.67, 31.37) * mm});
            skArc(sketch, "E52.2.9", {"start": v(-18.67, 31.37) * mm, "mid": v(-17.73, 30.63) * mm, "end": v(-16.53, 30.76) * mm});
            skArc(sketch, "E52.3.0", {"start": v(-28.34, 20.4) * mm, "mid": v(-28.06, 21.57) * mm, "end": v(-28.66, 22.6) * mm});
            skLineSegment(sketch, "E52.3.1", {"start": v(-30.06, 23.68) * mm, "end": v(-28.66, 22.6) * mm});
            skArc(sketch, "E52.3.2", {"start": v(-30.06, 23.68) * mm, "mid": v(-30.75, 25.1) * mm, "end": v(-31.2, 26.64) * mm});
            skLineSegment(sketch, "E52.3.3", {"start": v(-31.1, 27.05) * mm, "end": v(-31, 27.18) * mm});
            skArc(sketch, "E52.3.4", {"start": v(-31.1, 27.05) * mm, "mid": v(-31.2, 26.85) * mm, "end": v(-31.2, 26.64) * mm});
            skLineSegment(sketch, "E52.3.5", {"start": v(-30.88, 27.3) * mm, "end": v(-31, 27.18) * mm});
            skArc(sketch, "E52.3.6", {"start": v(-30.48, 27.45) * mm, "mid": v(-30.7, 27.42) * mm, "end": v(-30.88, 27.3) * mm});
            skArc(sketch, "E52.3.7", {"start": v(-27.4, 26.7) * mm, "mid": v(-28.91, 27.21) * mm, "end": v(-30.48, 27.45) * mm});
            skLineSegment(sketch, "E52.3.8", {"start": v(-27.4, 26.7) * mm, "end": v(-26.16, 25.47) * mm});
            skArc(sketch, "E52.3.9", {"start": v(-26.16, 25.47) * mm, "mid": v(-25.05, 25) * mm, "end": v(-23.93, 25.44) * mm});
            skArc(sketch, "E52.4.0", {"start": v(-32.66, 12.37) * mm, "mid": v(-32.69, 13.57) * mm, "end": v(-33.54, 14.42) * mm});
            skLineSegment(sketch, "E52.4.1", {"start": v(-35.16, 15.1) * mm, "end": v(-33.54, 14.42) * mm});
            skArc(sketch, "E52.4.2", {"start": v(-35.16, 15.1) * mm, "mid": v(-36.2, 16.3) * mm, "end": v(-37.03, 17.65) * mm});
            skLineSegment(sketch, "E52.4.3", {"start": v(-37.05, 18.07) * mm, "end": v(-36.98, 18.23) * mm});
            skArc(sketch, "E52.4.4", {"start": v(-37.05, 18.07) * mm, "mid": v(-37.08, 17.86) * mm, "end": v(-37.03, 17.65) * mm});
            skLineSegment(sketch, "E52.4.5", {"start": v(-36.9, 18.38) * mm, "end": v(-36.98, 18.23) * mm});
            skArc(sketch, "E52.4.6", {"start": v(-36.55, 18.63) * mm, "mid": v(-36.75, 18.54) * mm, "end": v(-36.9, 18.38) * mm});
            skArc(sketch, "E52.4.7", {"start": v(-33.38, 18.7) * mm, "mid": v(-34.97, 18.8) * mm, "end": v(-36.55, 18.63) * mm});
            skLineSegment(sketch, "E52.4.8", {"start": v(-33.38, 18.7) * mm, "end": v(-31.86, 17.83) * mm});
            skArc(sketch, "E52.4.9", {"start": v(-31.86, 17.83) * mm, "mid": v(-30.67, 17.67) * mm, "end": v(-29.7, 18.38) * mm});
            skArc(sketch, "E52.5.0", {"start": v(-34.75, 3.5) * mm, "mid": v(-35.09, 4.65) * mm, "end": v(-36.13, 5.24) * mm});
            skLineSegment(sketch, "E52.5.1", {"start": v(-37.87, 5.48) * mm, "end": v(-36.13, 5.24) * mm});
            skArc(sketch, "E52.5.2", {"start": v(-37.87, 5.48) * mm, "mid": v(-39.19, 6.37) * mm, "end": v(-40.34, 7.47) * mm});
            skLineSegment(sketch, "E52.5.3", {"start": v(-40.46, 7.87) * mm, "end": v(-40.44, 8.04) * mm});
            skArc(sketch, "E52.5.4", {"start": v(-40.46, 7.87) * mm, "mid": v(-40.44, 7.66) * mm, "end": v(-40.34, 7.47) * mm});
            skLineSegment(sketch, "E52.5.5", {"start": v(-40.4, 8.2) * mm, "end": v(-40.44, 8.04) * mm});
            skArc(sketch, "E52.5.6", {"start": v(-40.13, 8.53) * mm, "mid": v(-40.3, 8.4) * mm, "end": v(-40.4, 8.2) * mm});
            skArc(sketch, "E52.5.7", {"start": v(-37.09, 9.43) * mm, "mid": v(-38.64, 9.1) * mm, "end": v(-40.13, 8.53) * mm});
            skLineSegment(sketch, "E52.5.8", {"start": v(-37.09, 9.43) * mm, "end": v(-35.38, 8.98) * mm});
            skArc(sketch, "E52.5.9", {"start": v(-35.38, 8.98) * mm, "mid": v(-34.2, 9.13) * mm, "end": v(-33.44, 10.06) * mm});
            skArc(sketch, "E52.6.0", {"start": v(-34.47, -5.62) * mm, "mid": v(-35.1, -4.59) * mm, "end": v(-36.25, -4.29) * mm});
            skLineSegment(sketch, "E52.6.1", {"start": v(-38, -4.5) * mm, "end": v(-36.25, -4.29) * mm});
            skArc(sketch, "E52.6.2", {"start": v(-38, -4.5) * mm, "mid": v(-39.5, -4) * mm, "end": v(-40.9, -3.23) * mm});
            skLineSegment(sketch, "E52.6.3", {"start": v(-41.12, -2.87) * mm, "end": v(-41.14, -2.7) * mm});
            skArc(sketch, "E52.6.4", {"start": v(-41.12, -2.87) * mm, "mid": v(-41.05, -3.07) * mm, "end": v(-40.9, -3.23) * mm});
            skLineSegment(sketch, "E52.6.5", {"start": v(-41.14, -2.53) * mm, "end": v(-41.14, -2.7) * mm});
            skArc(sketch, "E52.6.6", {"start": v(-40.97, -2.14) * mm, "mid": v(-41.1, -2.32) * mm, "end": v(-41.14, -2.53) * mm});
            skArc(sketch, "E52.6.7", {"start": v(-38.26, -0.5) * mm, "mid": v(-39.69, -1.2) * mm, "end": v(-40.97, -2.14) * mm});
            skLineSegment(sketch, "E52.6.8", {"start": v(-38.26, -0.5) * mm, "end": v(-36.5, -0.49) * mm});
            skArc(sketch, "E52.6.9", {"start": v(-36.5, -0.49) * mm, "mid": v(-35.4, -0.03) * mm, "end": v(-34.9, 1.06) * mm});
            skArc(sketch, "E52.7.0", {"start": v(-31.84, -14.35) * mm, "mid": v(-32.7, -13.52) * mm, "end": v(-33.9, -13.52) * mm});
            skLineSegment(sketch, "E52.7.1", {"start": v(-35.54, -14.19) * mm, "end": v(-33.9, -13.52) * mm});
            skArc(sketch, "E52.7.2", {"start": v(-35.54, -14.19) * mm, "mid": v(-37.12, -14.08) * mm, "end": v(-38.67, -13.7) * mm});
            skLineSegment(sketch, "E52.7.3", {"start": v(-38.98, -13.42) * mm, "end": v(-39.04, -13.26) * mm});
            skArc(sketch, "E52.7.4", {"start": v(-38.98, -13.42) * mm, "mid": v(-38.85, -13.6) * mm, "end": v(-38.67, -13.7) * mm});
            skLineSegment(sketch, "E52.7.5", {"start": v(-39.09, -13.09) * mm, "end": v(-39.04, -13.26) * mm});
            skArc(sketch, "E52.7.6", {"start": v(-39.02, -12.67) * mm, "mid": v(-39.1, -12.87) * mm, "end": v(-39.09, -13.09) * mm});
            skArc(sketch, "E52.7.7", {"start": v(-36.83, -10.38) * mm, "mid": v(-38.02, -11.43) * mm, "end": v(-39.02, -12.67) * mm});
            skLineSegment(sketch, "E52.7.8", {"start": v(-36.83, -10.38) * mm, "end": v(-35.13, -9.92) * mm});
            skArc(sketch, "E52.7.9", {"start": v(-35.13, -9.92) * mm, "mid": v(-34.18, -9.2) * mm, "end": v(-34, -8) * mm});
            skArc(sketch, "E52.8.0", {"start": v(-27.04, -22.1) * mm, "mid": v(-28.1, -21.52) * mm, "end": v(-29.25, -21.84) * mm});
            skLineSegment(sketch, "E52.8.1", {"start": v(-30.65, -22.9) * mm, "end": v(-29.25, -21.84) * mm});
            skArc(sketch, "E52.8.2", {"start": v(-30.65, -22.9) * mm, "mid": v(-32.21, -23.2) * mm, "end": v(-33.8, -23.24) * mm});
            skLineSegment(sketch, "E52.8.3", {"start": v(-34.18, -23.05) * mm, "end": v(-34.28, -22.9) * mm});
            skArc(sketch, "E52.8.4", {"start": v(-34.18, -23.05) * mm, "mid": v(-34.01, -23.19) * mm, "end": v(-33.8, -23.24) * mm});
            skLineSegment(sketch, "E52.8.5", {"start": v(-34.37, -22.76) * mm, "end": v(-34.28, -22.9) * mm});
            skArc(sketch, "E52.8.6", {"start": v(-34.4, -22.34) * mm, "mid": v(-34.43, -22.55) * mm, "end": v(-34.37, -22.76) * mm});
            skArc(sketch, "E52.8.7", {"start": v(-32.89, -19.56) * mm, "mid": v(-33.77, -20.88) * mm, "end": v(-34.4, -22.34) * mm});
            skLineSegment(sketch, "E52.8.8", {"start": v(-32.89, -19.56) * mm, "end": v(-31.37, -18.67) * mm});
            skArc(sketch, "E52.8.9", {"start": v(-31.37, -18.67) * mm, "mid": v(-30.63, -17.73) * mm, "end": v(-30.76, -16.53) * mm});
            skArc(sketch, "E52.9.0", {"start": v(-20.4, -28.34) * mm, "mid": v(-21.57, -28.06) * mm, "end": v(-22.6, -28.66) * mm});
            skLineSegment(sketch, "E52.9.1", {"start": v(-23.68, -30.06) * mm, "end": v(-22.6, -28.66) * mm});
            skArc(sketch, "E52.9.2", {"start": v(-23.68, -30.06) * mm, "mid": v(-25.1, -30.75) * mm, "end": v(-26.64, -31.2) * mm});
            skLineSegment(sketch, "E52.9.3", {"start": v(-27.05, -31.1) * mm, "end": v(-27.18, -31) * mm});
            skArc(sketch, "E52.9.4", {"start": v(-27.05, -31.1) * mm, "mid": v(-26.85, -31.2) * mm, "end": v(-26.64, -31.2) * mm});
            skLineSegment(sketch, "E52.9.5", {"start": v(-27.3, -30.88) * mm, "end": v(-27.18, -31) * mm});
            skArc(sketch, "E52.9.6", {"start": v(-27.45, -30.48) * mm, "mid": v(-27.42, -30.7) * mm, "end": v(-27.3, -30.88) * mm});
            skArc(sketch, "E52.9.7", {"start": v(-26.7, -27.4) * mm, "mid": v(-27.21, -28.91) * mm, "end": v(-27.45, -30.48) * mm});
            skLineSegment(sketch, "E52.9.8", {"start": v(-26.7, -27.4) * mm, "end": v(-25.47, -26.16) * mm});
            skArc(sketch, "E52.9.9", {"start": v(-25.47, -26.16) * mm, "mid": v(-25, -25.05) * mm, "end": v(-25.44, -23.93) * mm});
            skArc(sketch, "E52.10.0", {"start": v(-12.37, -32.66) * mm, "mid": v(-13.57, -32.69) * mm, "end": v(-14.42, -33.54) * mm});
            skLineSegment(sketch, "E52.10.1", {"start": v(-15.1, -35.16) * mm, "end": v(-14.42, -33.54) * mm});
            skArc(sketch, "E52.10.2", {"start": v(-15.1, -35.16) * mm, "mid": v(-16.3, -36.2) * mm, "end": v(-17.65, -37.03) * mm});
            skLineSegment(sketch, "E52.10.3", {"start": v(-18.07, -37.05) * mm, "end": v(-18.23, -36.98) * mm});
            skArc(sketch, "E52.10.4", {"start": v(-18.07, -37.05) * mm, "mid": v(-17.86, -37.08) * mm, "end": v(-17.65, -37.03) * mm});
            skLineSegment(sketch, "E52.10.5", {"start": v(-18.38, -36.9) * mm, "end": v(-18.23, -36.98) * mm});
            skArc(sketch, "E52.10.6", {"start": v(-18.63, -36.55) * mm, "mid": v(-18.54, -36.75) * mm, "end": v(-18.38, -36.9) * mm});
            skArc(sketch, "E52.10.7", {"start": v(-18.7, -33.38) * mm, "mid": v(-18.8, -34.97) * mm, "end": v(-18.63, -36.55) * mm});
            skLineSegment(sketch, "E52.10.8", {"start": v(-18.7, -33.38) * mm, "end": v(-17.83, -31.86) * mm});
            skArc(sketch, "E52.10.9", {"start": v(-17.83, -31.86) * mm, "mid": v(-17.67, -30.67) * mm, "end": v(-18.38, -29.7) * mm});
            skArc(sketch, "E52.11.0", {"start": v(-3.5, -34.75) * mm, "mid": v(-4.65, -35.09) * mm, "end": v(-5.24, -36.13) * mm});
            skLineSegment(sketch, "E52.11.1", {"start": v(-5.48, -37.87) * mm, "end": v(-5.24, -36.13) * mm});
            skArc(sketch, "E52.11.2", {"start": v(-5.48, -37.87) * mm, "mid": v(-6.37, -39.19) * mm, "end": v(-7.47, -40.34) * mm});
            skLineSegment(sketch, "E52.11.3", {"start": v(-7.87, -40.46) * mm, "end": v(-8.04, -40.44) * mm});
            skArc(sketch, "E52.11.4", {"start": v(-7.87, -40.46) * mm, "mid": v(-7.66, -40.44) * mm, "end": v(-7.47, -40.34) * mm});
            skLineSegment(sketch, "E52.11.5", {"start": v(-8.2, -40.4) * mm, "end": v(-8.04, -40.44) * mm});
            skArc(sketch, "E52.11.6", {"start": v(-8.53, -40.13) * mm, "mid": v(-8.4, -40.3) * mm, "end": v(-8.2, -40.4) * mm});
            skArc(sketch, "E52.11.7", {"start": v(-9.43, -37.09) * mm, "mid": v(-9.1, -38.64) * mm, "end": v(-8.53, -40.13) * mm});
            skLineSegment(sketch, "E52.11.8", {"start": v(-9.43, -37.09) * mm, "end": v(-8.98, -35.38) * mm});
            skArc(sketch, "E52.11.9", {"start": v(-8.98, -35.38) * mm, "mid": v(-9.13, -34.2) * mm, "end": v(-10.06, -33.44) * mm});
            skArc(sketch, "E52.12.0", {"start": v(5.62, -34.47) * mm, "mid": v(4.59, -35.1) * mm, "end": v(4.29, -36.25) * mm});
            skLineSegment(sketch, "E52.12.1", {"start": v(4.5, -38) * mm, "end": v(4.29, -36.25) * mm});
            skArc(sketch, "E52.12.2", {"start": v(4.5, -38) * mm, "mid": v(4, -39.5) * mm, "end": v(3.23, -40.9) * mm});
            skLineSegment(sketch, "E52.12.3", {"start": v(2.87, -41.12) * mm, "end": v(2.7, -41.14) * mm});
            skArc(sketch, "E52.12.4", {"start": v(2.87, -41.12) * mm, "mid": v(3.07, -41.05) * mm, "end": v(3.23, -40.9) * mm});
            skLineSegment(sketch, "E52.12.5", {"start": v(2.53, -41.14) * mm, "end": v(2.7, -41.14) * mm});
            skArc(sketch, "E52.12.6", {"start": v(2.14, -40.97) * mm, "mid": v(2.32, -41.1) * mm, "end": v(2.53, -41.14) * mm});
            skArc(sketch, "E52.12.7", {"start": v(0.5, -38.26) * mm, "mid": v(1.2, -39.69) * mm, "end": v(2.14, -40.97) * mm});
            skLineSegment(sketch, "E52.12.8", {"start": v(0.5, -38.26) * mm, "end": v(0.49, -36.5) * mm});
            skArc(sketch, "E52.12.9", {"start": v(0.49, -36.5) * mm, "mid": v(0.03, -35.4) * mm, "end": v(-1.06, -34.9) * mm});
            skArc(sketch, "E52.13.0", {"start": v(14.35, -31.84) * mm, "mid": v(13.52, -32.7) * mm, "end": v(13.52, -33.9) * mm});
            skLineSegment(sketch, "E52.13.1", {"start": v(14.19, -35.54) * mm, "end": v(13.52, -33.9) * mm});
            skArc(sketch, "E52.13.2", {"start": v(14.19, -35.54) * mm, "mid": v(14.08, -37.12) * mm, "end": v(13.7, -38.67) * mm});
            skLineSegment(sketch, "E52.13.3", {"start": v(13.42, -38.98) * mm, "end": v(13.26, -39.04) * mm});
            skArc(sketch, "E52.13.4", {"start": v(13.42, -38.98) * mm, "mid": v(13.6, -38.85) * mm, "end": v(13.7, -38.67) * mm});
            skLineSegment(sketch, "E52.13.5", {"start": v(13.09, -39.09) * mm, "end": v(13.26, -39.04) * mm});
            skArc(sketch, "E52.13.6", {"start": v(12.67, -39.02) * mm, "mid": v(12.87, -39.1) * mm, "end": v(13.09, -39.09) * mm});
            skArc(sketch, "E52.13.7", {"start": v(10.38, -36.83) * mm, "mid": v(11.43, -38.02) * mm, "end": v(12.67, -39.02) * mm});
            skLineSegment(sketch, "E52.13.8", {"start": v(10.38, -36.83) * mm, "end": v(9.92, -35.13) * mm});
            skArc(sketch, "E52.13.9", {"start": v(9.92, -35.13) * mm, "mid": v(9.2, -34.18) * mm, "end": v(8, -34) * mm});
            skArc(sketch, "E52.14.0", {"start": v(22.1, -27.04) * mm, "mid": v(21.52, -28.1) * mm, "end": v(21.84, -29.25) * mm});
            skLineSegment(sketch, "E52.14.1", {"start": v(22.9, -30.65) * mm, "end": v(21.84, -29.25) * mm});
            skArc(sketch, "E52.14.2", {"start": v(22.9, -30.65) * mm, "mid": v(23.2, -32.21) * mm, "end": v(23.24, -33.8) * mm});
            skLineSegment(sketch, "E52.14.3", {"start": v(23.05, -34.18) * mm, "end": v(22.9, -34.28) * mm});
            skArc(sketch, "E52.14.4", {"start": v(23.05, -34.18) * mm, "mid": v(23.19, -34.01) * mm, "end": v(23.24, -33.8) * mm});
            skLineSegment(sketch, "E52.14.5", {"start": v(22.76, -34.37) * mm, "end": v(22.9, -34.28) * mm});
            skArc(sketch, "E52.14.6", {"start": v(22.34, -34.4) * mm, "mid": v(22.55, -34.43) * mm, "end": v(22.76, -34.37) * mm});
            skArc(sketch, "E52.14.7", {"start": v(19.56, -32.89) * mm, "mid": v(20.88, -33.77) * mm, "end": v(22.34, -34.4) * mm});
            skLineSegment(sketch, "E52.14.8", {"start": v(19.56, -32.89) * mm, "end": v(18.67, -31.37) * mm});
            skArc(sketch, "E52.14.9", {"start": v(18.67, -31.37) * mm, "mid": v(17.73, -30.63) * mm, "end": v(16.53, -30.76) * mm});
            skArc(sketch, "E52.15.0", {"start": v(28.34, -20.4) * mm, "mid": v(28.06, -21.57) * mm, "end": v(28.66, -22.6) * mm});
            skLineSegment(sketch, "E52.15.1", {"start": v(30.06, -23.68) * mm, "end": v(28.66, -22.6) * mm});
            skArc(sketch, "E52.15.2", {"start": v(30.06, -23.68) * mm, "mid": v(30.75, -25.1) * mm, "end": v(31.2, -26.64) * mm});
            skLineSegment(sketch, "E52.15.3", {"start": v(31.1, -27.05) * mm, "end": v(31, -27.18) * mm});
            skArc(sketch, "E52.15.4", {"start": v(31.1, -27.05) * mm, "mid": v(31.2, -26.85) * mm, "end": v(31.2, -26.64) * mm});
            skLineSegment(sketch, "E52.15.5", {"start": v(30.88, -27.3) * mm, "end": v(31, -27.18) * mm});
            skArc(sketch, "E52.15.6", {"start": v(30.48, -27.45) * mm, "mid": v(30.7, -27.42) * mm, "end": v(30.88, -27.3) * mm});
            skArc(sketch, "E52.15.7", {"start": v(27.4, -26.7) * mm, "mid": v(28.91, -27.21) * mm, "end": v(30.48, -27.45) * mm});
            skLineSegment(sketch, "E52.15.8", {"start": v(27.4, -26.7) * mm, "end": v(26.16, -25.47) * mm});
            skArc(sketch, "E52.15.9", {"start": v(26.16, -25.47) * mm, "mid": v(25.05, -25) * mm, "end": v(23.93, -25.44) * mm});
            skArc(sketch, "E52.16.0", {"start": v(32.66, -12.37) * mm, "mid": v(32.69, -13.57) * mm, "end": v(33.54, -14.42) * mm});
            skLineSegment(sketch, "E52.16.1", {"start": v(35.16, -15.1) * mm, "end": v(33.54, -14.42) * mm});
            skArc(sketch, "E52.16.2", {"start": v(35.16, -15.1) * mm, "mid": v(36.2, -16.3) * mm, "end": v(37.03, -17.65) * mm});
            skLineSegment(sketch, "E52.16.3", {"start": v(37.05, -18.07) * mm, "end": v(36.98, -18.23) * mm});
            skArc(sketch, "E52.16.4", {"start": v(37.05, -18.07) * mm, "mid": v(37.08, -17.86) * mm, "end": v(37.03, -17.65) * mm});
            skLineSegment(sketch, "E52.16.5", {"start": v(36.9, -18.38) * mm, "end": v(36.98, -18.23) * mm});
            skArc(sketch, "E52.16.6", {"start": v(36.55, -18.63) * mm, "mid": v(36.75, -18.54) * mm, "end": v(36.9, -18.38) * mm});
            skArc(sketch, "E52.16.7", {"start": v(33.38, -18.7) * mm, "mid": v(34.97, -18.8) * mm, "end": v(36.55, -18.63) * mm});
            skLineSegment(sketch, "E52.16.8", {"start": v(33.38, -18.7) * mm, "end": v(31.86, -17.83) * mm});
            skArc(sketch, "E52.16.9", {"start": v(31.86, -17.83) * mm, "mid": v(30.67, -17.67) * mm, "end": v(29.7, -18.38) * mm});
            skArc(sketch, "E52.17.0", {"start": v(34.75, -3.5) * mm, "mid": v(35.09, -4.65) * mm, "end": v(36.13, -5.24) * mm});
            skLineSegment(sketch, "E52.17.1", {"start": v(37.87, -5.48) * mm, "end": v(36.13, -5.24) * mm});
            skArc(sketch, "E52.17.2", {"start": v(37.87, -5.48) * mm, "mid": v(39.19, -6.37) * mm, "end": v(40.34, -7.47) * mm});
            skLineSegment(sketch, "E52.17.3", {"start": v(40.46, -7.87) * mm, "end": v(40.44, -8.04) * mm});
            skArc(sketch, "E52.17.4", {"start": v(40.46, -7.87) * mm, "mid": v(40.44, -7.66) * mm, "end": v(40.34, -7.47) * mm});
            skLineSegment(sketch, "E52.17.5", {"start": v(40.4, -8.2) * mm, "end": v(40.44, -8.04) * mm});
            skArc(sketch, "E52.17.6", {"start": v(40.13, -8.53) * mm, "mid": v(40.3, -8.4) * mm, "end": v(40.4, -8.2) * mm});
            skArc(sketch, "E52.17.7", {"start": v(37.09, -9.43) * mm, "mid": v(38.64, -9.1) * mm, "end": v(40.13, -8.53) * mm});
            skLineSegment(sketch, "E52.17.8", {"start": v(37.09, -9.43) * mm, "end": v(35.38, -8.98) * mm});
            skArc(sketch, "E52.17.9", {"start": v(35.38, -8.98) * mm, "mid": v(34.2, -9.13) * mm, "end": v(33.44, -10.06) * mm});
            skArc(sketch, "E52.18.0", {"start": v(34.47, 5.62) * mm, "mid": v(35.1, 4.59) * mm, "end": v(36.25, 4.29) * mm});
            skLineSegment(sketch, "E52.18.1", {"start": v(38, 4.5) * mm, "end": v(36.25, 4.29) * mm});
            skArc(sketch, "E52.18.2", {"start": v(38, 4.5) * mm, "mid": v(39.5, 4) * mm, "end": v(40.9, 3.23) * mm});
            skLineSegment(sketch, "E52.18.3", {"start": v(41.12, 2.87) * mm, "end": v(41.14, 2.7) * mm});
            skArc(sketch, "E52.18.4", {"start": v(41.12, 2.87) * mm, "mid": v(41.05, 3.07) * mm, "end": v(40.9, 3.23) * mm});
            skLineSegment(sketch, "E52.18.5", {"start": v(41.14, 2.53) * mm, "end": v(41.14, 2.7) * mm});
            skArc(sketch, "E52.18.6", {"start": v(40.97, 2.14) * mm, "mid": v(41.1, 2.32) * mm, "end": v(41.14, 2.53) * mm});
            skArc(sketch, "E52.18.7", {"start": v(38.26, 0.5) * mm, "mid": v(39.69, 1.2) * mm, "end": v(40.97, 2.14) * mm});
            skLineSegment(sketch, "E52.18.8", {"start": v(38.26, 0.5) * mm, "end": v(36.5, 0.49) * mm});
            skArc(sketch, "E52.18.9", {"start": v(36.5, 0.49) * mm, "mid": v(35.4, 0.03) * mm, "end": v(34.9, -1.06) * mm});
            skArc(sketch, "E52.19.0", {"start": v(31.84, 14.35) * mm, "mid": v(32.7, 13.52) * mm, "end": v(33.9, 13.52) * mm});
            skLineSegment(sketch, "E52.19.1", {"start": v(35.54, 14.19) * mm, "end": v(33.9, 13.52) * mm});
            skArc(sketch, "E52.19.2", {"start": v(35.54, 14.19) * mm, "mid": v(37.12, 14.08) * mm, "end": v(38.67, 13.7) * mm});
            skLineSegment(sketch, "E52.19.3", {"start": v(38.98, 13.42) * mm, "end": v(39.04, 13.26) * mm});
            skArc(sketch, "E52.19.4", {"start": v(38.98, 13.42) * mm, "mid": v(38.85, 13.6) * mm, "end": v(38.67, 13.7) * mm});
            skLineSegment(sketch, "E52.19.5", {"start": v(39.09, 13.09) * mm, "end": v(39.04, 13.26) * mm});
            skArc(sketch, "E52.19.6", {"start": v(39.02, 12.67) * mm, "mid": v(39.1, 12.87) * mm, "end": v(39.09, 13.09) * mm});
            skArc(sketch, "E52.19.7", {"start": v(36.83, 10.38) * mm, "mid": v(38.02, 11.43) * mm, "end": v(39.02, 12.67) * mm});
            skLineSegment(sketch, "E52.19.8", {"start": v(36.83, 10.38) * mm, "end": v(35.13, 9.92) * mm});
            skArc(sketch, "E52.19.9", {"start": v(35.13, 9.92) * mm, "mid": v(34.18, 9.2) * mm, "end": v(34, 8) * mm});
            skArc(sketch, "E52.20.0", {"start": v(27.04, 22.1) * mm, "mid": v(28.1, 21.52) * mm, "end": v(29.25, 21.84) * mm});
            skLineSegment(sketch, "E52.20.1", {"start": v(30.65, 22.9) * mm, "end": v(29.25, 21.84) * mm});
            skArc(sketch, "E52.20.2", {"start": v(30.65, 22.9) * mm, "mid": v(32.21, 23.2) * mm, "end": v(33.8, 23.24) * mm});
            skLineSegment(sketch, "E52.20.3", {"start": v(34.18, 23.05) * mm, "end": v(34.28, 22.9) * mm});
            skArc(sketch, "E52.20.4", {"start": v(34.18, 23.05) * mm, "mid": v(34.01, 23.19) * mm, "end": v(33.8, 23.24) * mm});
            skLineSegment(sketch, "E52.20.5", {"start": v(34.37, 22.76) * mm, "end": v(34.28, 22.9) * mm});
            skArc(sketch, "E52.20.6", {"start": v(34.4, 22.34) * mm, "mid": v(34.43, 22.55) * mm, "end": v(34.37, 22.76) * mm});
            skArc(sketch, "E52.20.7", {"start": v(32.89, 19.56) * mm, "mid": v(33.77, 20.88) * mm, "end": v(34.4, 22.34) * mm});
            skLineSegment(sketch, "E52.20.8", {"start": v(32.89, 19.56) * mm, "end": v(31.37, 18.67) * mm});
            skArc(sketch, "E52.20.9", {"start": v(31.37, 18.67) * mm, "mid": v(30.63, 17.73) * mm, "end": v(30.76, 16.53) * mm});
            skArc(sketch, "E52.21.0", {"start": v(20.4, 28.34) * mm, "mid": v(21.57, 28.06) * mm, "end": v(22.6, 28.66) * mm});
            skLineSegment(sketch, "E52.21.1", {"start": v(23.68, 30.06) * mm, "end": v(22.6, 28.66) * mm});
            skArc(sketch, "E52.21.2", {"start": v(23.68, 30.06) * mm, "mid": v(25.1, 30.75) * mm, "end": v(26.64, 31.2) * mm});
            skLineSegment(sketch, "E52.21.3", {"start": v(27.05, 31.1) * mm, "end": v(27.18, 31) * mm});
            skArc(sketch, "E52.21.4", {"start": v(27.05, 31.1) * mm, "mid": v(26.85, 31.2) * mm, "end": v(26.64, 31.2) * mm});
            skLineSegment(sketch, "E52.21.5", {"start": v(27.3, 30.88) * mm, "end": v(27.18, 31) * mm});
            skArc(sketch, "E52.21.6", {"start": v(27.45, 30.48) * mm, "mid": v(27.42, 30.7) * mm, "end": v(27.3, 30.88) * mm});
            skArc(sketch, "E52.21.7", {"start": v(26.7, 27.4) * mm, "mid": v(27.21, 28.91) * mm, "end": v(27.45, 30.48) * mm});
            skLineSegment(sketch, "E52.21.8", {"start": v(26.7, 27.4) * mm, "end": v(25.47, 26.16) * mm});
            skArc(sketch, "E52.21.9", {"start": v(25.47, 26.16) * mm, "mid": v(25, 25.05) * mm, "end": v(25.44, 23.93) * mm});
            skArc(sketch, "E52.22.0", {"start": v(12.37, 32.66) * mm, "mid": v(13.57, 32.69) * mm, "end": v(14.42, 33.54) * mm});
            skLineSegment(sketch, "E52.22.1", {"start": v(15.1, 35.16) * mm, "end": v(14.42, 33.54) * mm});
            skArc(sketch, "E52.22.2", {"start": v(15.1, 35.16) * mm, "mid": v(16.3, 36.2) * mm, "end": v(17.65, 37.03) * mm});
            skLineSegment(sketch, "E52.22.3", {"start": v(18.07, 37.05) * mm, "end": v(18.23, 36.98) * mm});
            skArc(sketch, "E52.22.4", {"start": v(18.07, 37.05) * mm, "mid": v(17.86, 37.08) * mm, "end": v(17.65, 37.03) * mm});
            skLineSegment(sketch, "E52.22.5", {"start": v(18.38, 36.9) * mm, "end": v(18.23, 36.98) * mm});
            skArc(sketch, "E52.22.6", {"start": v(18.63, 36.55) * mm, "mid": v(18.54, 36.75) * mm, "end": v(18.38, 36.9) * mm});
            skArc(sketch, "E52.22.7", {"start": v(18.7, 33.38) * mm, "mid": v(18.8, 34.97) * mm, "end": v(18.63, 36.55) * mm});
            skLineSegment(sketch, "E52.22.8", {"start": v(18.7, 33.38) * mm, "end": v(17.83, 31.86) * mm});
            skArc(sketch, "E52.22.9", {"start": v(17.83, 31.86) * mm, "mid": v(17.67, 30.67) * mm, "end": v(18.38, 29.7) * mm});
            skArc(sketch, "E52.23.0", {"start": v(3.5, 34.75) * mm, "mid": v(4.65, 35.09) * mm, "end": v(5.24, 36.13) * mm});
            skLineSegment(sketch, "E52.23.1", {"start": v(5.48, 37.87) * mm, "end": v(5.24, 36.13) * mm});
            skArc(sketch, "E52.23.2", {"start": v(5.48, 37.87) * mm, "mid": v(6.37, 39.19) * mm, "end": v(7.47, 40.34) * mm});
            skLineSegment(sketch, "E52.23.3", {"start": v(7.87, 40.46) * mm, "end": v(8.04, 40.44) * mm});
            skArc(sketch, "E52.23.4", {"start": v(7.87, 40.46) * mm, "mid": v(7.66, 40.44) * mm, "end": v(7.47, 40.34) * mm});
            skLineSegment(sketch, "E52.23.5", {"start": v(8.2, 40.4) * mm, "end": v(8.04, 40.44) * mm});
            skArc(sketch, "E52.23.6", {"start": v(8.53, 40.13) * mm, "mid": v(8.4, 40.3) * mm, "end": v(8.2, 40.4) * mm});
            skArc(sketch, "E52.23.7", {"start": v(9.43, 37.09) * mm, "mid": v(9.1, 38.64) * mm, "end": v(8.53, 40.13) * mm});
            skLineSegment(sketch, "E52.23.8", {"start": v(9.43, 37.09) * mm, "end": v(8.98, 35.38) * mm});
            skArc(sketch, "E52.23.9", {"start": v(8.98, 35.38) * mm, "mid": v(9.13, 34.2) * mm, "end": v(10.06, 33.44) * mm});
            skArc(sketch, "E53.trimOffspring", {"start": v(-14.35, 31.84) * mm, "mid": v(-15.45, 31.32) * mm, "end": v(-16.53, 30.76) * mm});
            skArc(sketch, "E54.trimOffspring", {"start": v(-22.1, 27.04) * mm, "mid": v(-23.03, 26.26) * mm, "end": v(-23.93, 25.44) * mm});
            skArc(sketch, "E55.trimOffspring", {"start": v(-28.34, 20.4) * mm, "mid": v(-29.04, 19.4) * mm, "end": v(-29.7, 18.38) * mm});
            skArc(sketch, "E56.trimOffspring", {"start": v(3.5, 34.75) * mm, "mid": v(2.28, 34.85) * mm, "end": v(1.06, 34.9) * mm});
            skArc(sketch, "E57.trimOffspring", {"start": v(12.37, 32.66) * mm, "mid": v(11.22, 33.07) * mm, "end": v(10.06, 33.44) * mm});
            skArc(sketch, "E58.trimOffspring", {"start": v(20.4, 28.34) * mm, "mid": v(19.4, 29.04) * mm, "end": v(18.38, 29.7) * mm});
            skArc(sketch, "E59.trimOffspring", {"start": v(27.04, 22.1) * mm, "mid": v(26.26, 23.03) * mm, "end": v(25.44, 23.93) * mm});
            skArc(sketch, "E60.trimOffspring", {"start": v(-32.66, 12.37) * mm, "mid": v(-33.07, 11.22) * mm, "end": v(-33.44, 10.06) * mm});
            skArc(sketch, "E61.trimOffspring", {"start": v(-34.75, 3.5) * mm, "mid": v(-34.85, 2.28) * mm, "end": v(-34.9, 1.06) * mm});
            skArc(sketch, "E62.trimOffspring", {"start": v(-34.47, -5.62) * mm, "mid": v(-34.25, -6.82) * mm, "end": v(-34, -8) * mm});
            skArc(sketch, "E63.trimOffspring", {"start": v(-31.84, -14.35) * mm, "mid": v(-31.32, -15.45) * mm, "end": v(-30.76, -16.53) * mm});
            skArc(sketch, "E64.trimOffspring", {"start": v(-27.04, -22.1) * mm, "mid": v(-26.26, -23.03) * mm, "end": v(-25.44, -23.93) * mm});
            skArc(sketch, "E65.trimOffspring", {"start": v(-20.4, -28.34) * mm, "mid": v(-19.4, -29.04) * mm, "end": v(-18.38, -29.7) * mm});
            skArc(sketch, "E66.trimOffspring", {"start": v(-12.37, -32.66) * mm, "mid": v(-11.22, -33.07) * mm, "end": v(-10.06, -33.44) * mm});
            skArc(sketch, "E67.trimOffspring", {"start": v(31.84, 14.35) * mm, "mid": v(31.32, 15.45) * mm, "end": v(30.76, 16.53) * mm});
            skArc(sketch, "E68.trimOffspring", {"start": v(34.47, 5.62) * mm, "mid": v(34.25, 6.82) * mm, "end": v(34, 8) * mm});
            skArc(sketch, "E69.trimOffspring", {"start": v(34.75, -3.5) * mm, "mid": v(34.85, -2.28) * mm, "end": v(34.9, -1.06) * mm});
            skArc(sketch, "E70.trimOffspring", {"start": v(32.66, -12.37) * mm, "mid": v(33.07, -11.22) * mm, "end": v(33.44, -10.06) * mm});
            skArc(sketch, "E71.trimOffspring", {"start": v(28.34, -20.4) * mm, "mid": v(29.04, -19.4) * mm, "end": v(29.7, -18.38) * mm});
            skArc(sketch, "E72.trimOffspring", {"start": v(22.1, -27.04) * mm, "mid": v(23.03, -26.26) * mm, "end": v(23.93, -25.44) * mm});
            skArc(sketch, "E73.trimOffspring", {"start": v(14.35, -31.84) * mm, "mid": v(15.45, -31.32) * mm, "end": v(16.53, -30.76) * mm});
            skArc(sketch, "E74.trimOffspring", {"start": v(5.62, -34.47) * mm, "mid": v(6.82, -34.25) * mm, "end": v(8, -34) * mm});
            skArc(sketch, "E75.trimOffspring", {"start": v(-3.5, -34.75) * mm, "mid": v(-2.28, -34.85) * mm, "end": v(-1.06, -34.9) * mm});
            skSolve(sketch);
        }
        {
            var Q0;
            Q0=makeQuery(id+"F0.imprint","IMPRINT",FACE,{"disambiguationData":[TD([[makeQuery(id+"F0.imprint","IMPRINT",EDGE,{"derivedFrom":sQuery(id+"F0.wireOp",EDGE,"E0")}),1.0]])]});
            var Q1;
            Q1=makeQuery(id+"F2.imprint","IMPRINT",FACE,{"disambiguationData":[TD([[makeQuery(id+"F2.imprint","IMPRINT",EDGE,{"derivedFrom":sQuery(id+"F2.wireOp",EDGE,"E38")}),1.0]])]});
            var Q2;
            Q2=sQuery(id+"F0.wireOp",VERTEX,"E5.MirrorCS.start");
            var Q3;
            Q3=sQuery(id+"F2.wireOp",VERTEX,"E52.23.4.start");
            loft(context, id + "F3", {"sheetProfilesArray" : [{ "sheetProfileEntities" : qUnion([Q0]) }, { "sheetProfileEntities" : qUnion([Q1]) }], "matchConnections" : true, "connections" : [{ "connectionEntities" : qUnion([Q2, Q3]), "connectionEdgeQueries" : qUnion([]), "connectionEdgeParameters" : [] }]});
        }
        {
            var Q0;
            Q0=makeQuery(id+"F3.opLoft","CAP_FACE",FACE,{"disambiguationData":[OSD([makeQuery(id+"F2.imprint","IMPRINT",FACE,{"disambiguationData":[TD([[makeQuery(id+"F2.imprint","IMPRINT",EDGE,{"derivedFrom":sQuery(id+"F2.wireOp",EDGE,"E38")}),1.0]])]})])],"isStart":true});
            var sketch = newSketch(context, id + "F4", { "sketchPlane" : qUnion([Q0])});
            skCircle(sketch, "E76", {"center": v(0, 0) * mm, "radius": 6.35 * mm});
            skSolve(sketch);
        }
        {
            var Q0;
            Q0 = qSketchRegion(id + "F4", true);
            extrude(context, id + "F5", {"entities" : qUnion([Q0]), "operationType" : NewBodyOperationType.REMOVE, "endBound" : BoundingType.THROUGH_ALL, "oppositeDirection" : true, "depth" : 25.4 * mm});
        }
    });
